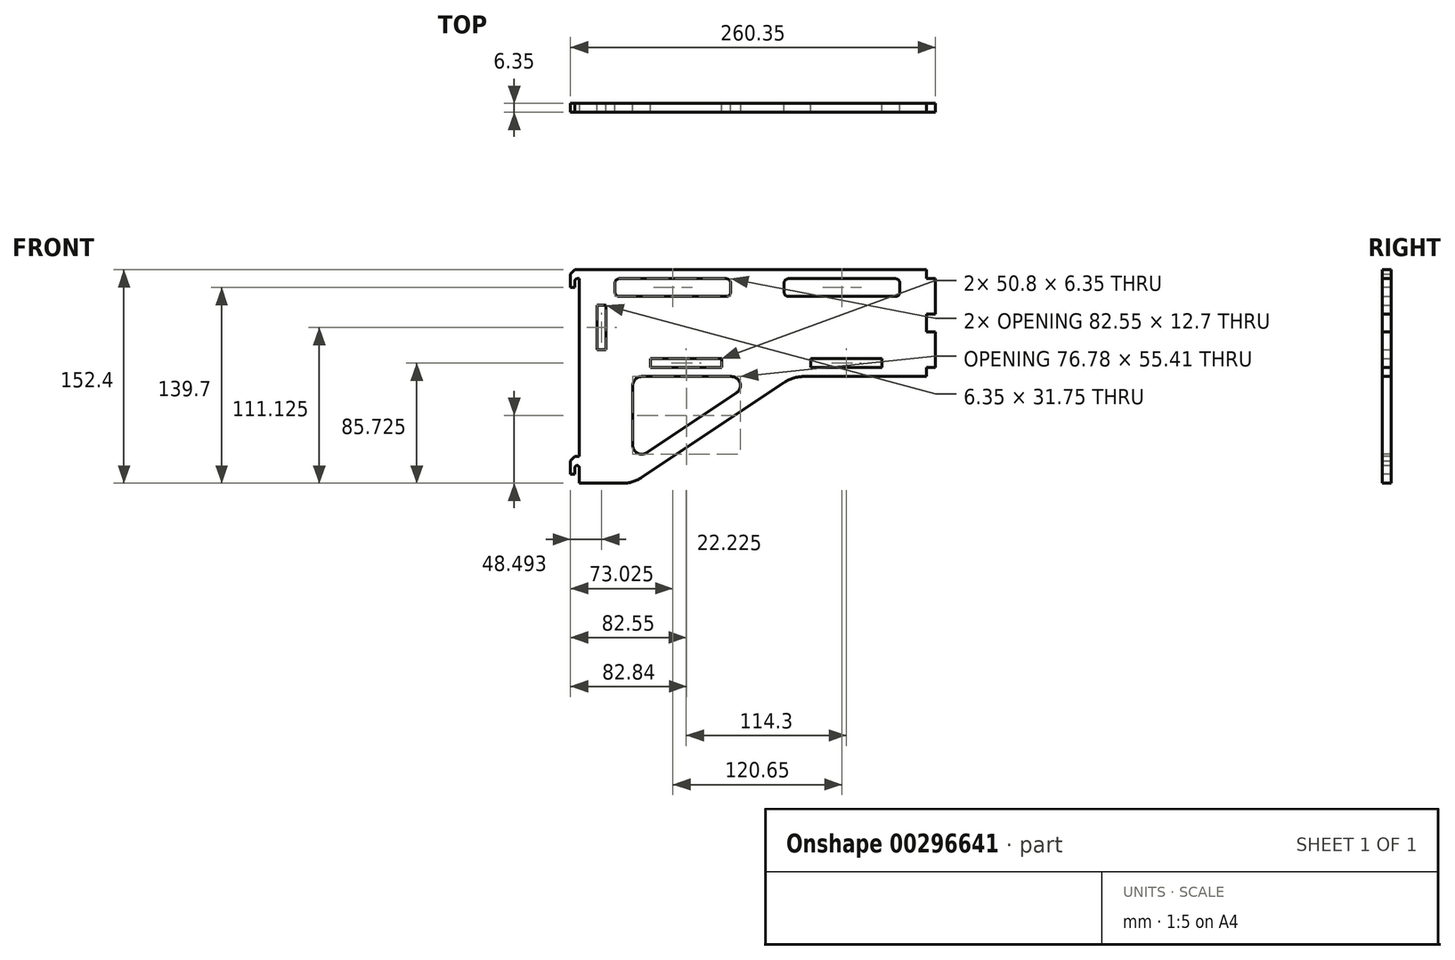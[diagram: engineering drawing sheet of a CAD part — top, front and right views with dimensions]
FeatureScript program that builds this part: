
annotation { "Feature Type Name" : "Feature", "Feature Type Description" : "" }
export const myFeature = defineFeature(function(context is Context, id is Id, definition is map)
    precondition{}
    {
        {
            var Q0;
            Q0=qCreatedBy(makeId("Front.planeOp"),FACE);
            var sketch = newSketch(context, id + "F0", { "sketchPlane" : qUnion([Q0])});
            skLineSegment(sketch, "E0.bottom", {"start": v(-127, 76.2) * mm, "end": v(120.65, 76.2) * mm});
            skLineSegment(sketch, "E0.top", {"start": v(-127, -76.2) * mm, "end": v(-88.9, -76.2) * mm});
            skLineSegment(sketch, "E0.left", {"start": v(-127, 76.2) * mm, "end": v(-127, -76.2) * mm});
            skLineSegment(sketch, "E0.right", {"start": v(127, 69.85) * mm, "end": v(127, 44.45) * mm});
            skPoint(sketch, "E0.middle", {"position": v(0, 0) * mm});
            skLineSegment(sketch, "E1", {"start": v(-88.9, -76.2) * mm, "end": v(25.4, 0) * mm});
            skLineSegment(sketch, "E2", {"start": v(25.4, 0) * mm, "end": v(120.65, 0) * mm});
            skPoint(sketch, "E3.orphan", {"position": v(127, -76.2) * mm});
            skPoint(sketch, "E4", {"position": v(0, 76.2) * mm});
            skPoint(sketch, "E5", {"position": v(-127, 0) * mm});
            skLineSegment(sketch, "E6.bottom", {"start": v(127, 69.85) * mm, "end": v(120.65, 69.85) * mm});
            skLineSegment(sketch, "E6.top", {"start": v(127, 44.45) * mm, "end": v(120.65, 44.45) * mm});
            skLineSegment(sketch, "E7.bottom", {"start": v(127, 31.75) * mm, "end": v(120.65, 31.75) * mm});
            skLineSegment(sketch, "E7.top", {"start": v(127, 6.35) * mm, "end": v(120.65, 6.35) * mm});
            skLineSegment(sketch, "E7.left", {"start": v(127, 31.75) * mm, "end": v(127, 6.35) * mm});
            skLineSegment(sketch, "E8", {"start": v(127, 38.1) * mm, "end": v(-127, 38.1) * mm, "construction": true});
            skLineSegment(sketch, "E9", {"start": v(120.65, 76.2) * mm, "end": v(120.65, 69.85) * mm});
            skPoint(sketch, "E10.orphan", {"position": v(127, 0) * mm});
            skPoint(sketch, "E11.orphan", {"position": v(127, 76.2) * mm});
            skLineSegment(sketch, "E12.trimOffspring", {"start": v(120.65, 44.45) * mm, "end": v(120.65, 31.75) * mm});
            skLineSegment(sketch, "E13.trimOffspring", {"start": v(120.65, 6.35) * mm, "end": v(120.65, 0) * mm});
            skPoint(sketch, "E14", {"position": v(127, 57.15) * mm});
            skPoint(sketch, "E15", {"position": v(127, 19.05) * mm});
            skLineSegment(sketch, "E16", {"start": v(127, 9.53) * mm, "end": v(-127, 9.52) * mm, "construction": true});
            skLineSegment(sketch, "E17.bottom", {"start": v(38.1, 12.7) * mm, "end": v(88.9, 12.7) * mm});
            skLineSegment(sketch, "E17.top", {"start": v(38.1, 6.35) * mm, "end": v(88.9, 6.35) * mm});
            skLineSegment(sketch, "E17.left", {"start": v(38.1, 12.7) * mm, "end": v(38.1, 6.35) * mm});
            skLineSegment(sketch, "E17.right", {"start": v(88.9, 12.7) * mm, "end": v(88.9, 6.35) * mm});
            skPoint(sketch, "E17.middle", {"position": v(63.5, 9.53) * mm});
            skLineSegment(sketch, "E18.bottom", {"start": v(-25.4, 12.7) * mm, "end": v(-76.2, 12.7) * mm});
            skLineSegment(sketch, "E18.top", {"start": v(-25.4, 6.35) * mm, "end": v(-76.2, 6.35) * mm});
            skLineSegment(sketch, "E18.left", {"start": v(-25.4, 12.7) * mm, "end": v(-25.4, 6.35) * mm});
            skLineSegment(sketch, "E18.right", {"start": v(-76.2, 12.7) * mm, "end": v(-76.2, 6.35) * mm});
            skPoint(sketch, "E18.middle", {"position": v(-50.8, 9.52) * mm});
            skLineSegment(sketch, "E19", {"start": v(-88.9, -60.94) * mm, "end": v(2.5, 0) * mm});
            skLineSegment(sketch, "E20", {"start": v(2.5, 0) * mm, "end": v(-88.9, 0) * mm});
            skLineSegment(sketch, "E21", {"start": v(-88.9, 0) * mm, "end": v(-88.9, -60.94) * mm});
            skLineSegment(sketch, "E22.bottom", {"start": v(-101.6, 69.85) * mm, "end": v(-19.05, 69.85) * mm});
            skLineSegment(sketch, "E22.top", {"start": v(-101.6, 57.15) * mm, "end": v(-19.05, 57.15) * mm});
            skLineSegment(sketch, "E22.left", {"start": v(-101.6, 69.85) * mm, "end": v(-101.6, 57.15) * mm});
            skLineSegment(sketch, "E22.right", {"start": v(-19.05, 69.85) * mm, "end": v(-19.05, 57.15) * mm});
            skLineSegment(sketch, "E23.MirrorCS", {"start": v(101.6, 69.85) * mm, "end": v(101.6, 57.15) * mm});
            skLineSegment(sketch, "E24.MirrorCS", {"start": v(101.6, 69.85) * mm, "end": v(19.05, 69.85) * mm});
            skLineSegment(sketch, "E25.MirrorCS", {"start": v(19.05, 69.85) * mm, "end": v(19.05, 57.15) * mm});
            skLineSegment(sketch, "E26.MirrorCS", {"start": v(101.6, 57.15) * mm, "end": v(19.05, 57.15) * mm});
            skPoint(sketch, "E27", {"position": v(6.35, 9.53) * mm});
            skPoint(sketch, "E28", {"position": v(-107.95, 9.52) * mm});
            skPoint(sketch, "E29", {"position": v(-111.13, 9.52) * mm});
            skLineSegment(sketch, "E30", {"start": v(-111.13, 76.2) * mm, "end": v(-111.13, -76.2) * mm, "construction": true});
            skLineSegment(sketch, "E31.bottom", {"start": v(-114.3, 50.8) * mm, "end": v(-107.95, 50.8) * mm});
            skLineSegment(sketch, "E31.top", {"start": v(-114.3, 19.05) * mm, "end": v(-107.95, 19.05) * mm});
            skLineSegment(sketch, "E31.left", {"start": v(-114.3, 50.8) * mm, "end": v(-114.3, 19.05) * mm});
            skLineSegment(sketch, "E31.right", {"start": v(-107.95, 50.8) * mm, "end": v(-107.95, 19.05) * mm});
            skPoint(sketch, "E31.middle", {"position": v(-111.13, 34.92) * mm});
            skSolve(sketch);
        }
        {
            var Q0;
            Q0 = qSketchRegion(id + "F0", true);
            extrude(context, id + "F1", {"entities" : qUnion([Q0]), "depth" : 6.35 * mm});
        }
        {
            var Q0;
            Q0=makeQuery(id+"F1.opExtrude","SWEPT_EDGE",EDGE,{"disambiguationData":[OSD([sQuery(id+"F0.wireOp",EDGE,"E19"),sQuery(id+"F0.wireOp",EDGE,"E20")])]});
            var Q1;
            Q1=makeQuery(id+"F1.opExtrude","SWEPT_EDGE",EDGE,{"disambiguationData":[OSD([sQuery(id+"F0.wireOp",EDGE,"E19"),sQuery(id+"F0.wireOp",EDGE,"E21")])]});
            var Q2;
            Q2=makeQuery(id+"F1.opExtrude","SWEPT_EDGE",EDGE,{"disambiguationData":[OSD([sQuery(id+"F0.wireOp",EDGE,"E20"),sQuery(id+"F0.wireOp",EDGE,"E21")])]});
            fillet(context, id + "F2", {"entities" : qUnion([Q0, Q1, Q2]), "radius" : 6.35 * mm, "tangentPropagation" : true, "allowEdgeOverflow" : false});
        }
        {
            var Q0;
            Q0=makeQuery(id+"F1.opExtrude","SWEPT_EDGE",EDGE,{"disambiguationData":[OSD([sQuery(id+"F0.wireOp",EDGE,"E1"),sQuery(id+"F0.wireOp",EDGE,"E2")])]});
            var Q1;
            Q1=makeQuery(id+"F1.opExtrude","SWEPT_EDGE",EDGE,{"disambiguationData":[OSD([sQuery(id+"F0.wireOp",EDGE,"E0.top"),sQuery(id+"F0.wireOp",EDGE,"E1")])]});
            fillet(context, id + "F3", {"entities" : qUnion([Q0, Q1]), "radius" : 25.4 * mm, "tangentPropagation" : true, "allowEdgeOverflow" : false});
        }
        {
            var Q0;
            Q0=makeQuery(id+"F1.opExtrude","SWEPT_EDGE",EDGE,{"disambiguationData":[OSD([sQuery(id+"F0.wireOp",EDGE,"E22.top"),sQuery(id+"F0.wireOp",EDGE,"E22.left")])]});
            var Q1;
            Q1=makeQuery(id+"F1.opExtrude","SWEPT_EDGE",EDGE,{"disambiguationData":[OSD([sQuery(id+"F0.wireOp",EDGE,"E22.bottom"),sQuery(id+"F0.wireOp",EDGE,"E22.left")])]});
            var Q2;
            Q2=makeQuery(id+"F1.opExtrude","SWEPT_EDGE",EDGE,{"disambiguationData":[OSD([sQuery(id+"F0.wireOp",EDGE,"E22.top"),sQuery(id+"F0.wireOp",EDGE,"E22.right")])]});
            var Q3;
            Q3=makeQuery(id+"F1.opExtrude","SWEPT_EDGE",EDGE,{"disambiguationData":[OSD([sQuery(id+"F0.wireOp",EDGE,"E22.bottom"),sQuery(id+"F0.wireOp",EDGE,"E22.right")])]});
            var Q4;
            Q4=makeQuery(id+"F1.opExtrude","SWEPT_EDGE",EDGE,{"disambiguationData":[OSD([sQuery(id+"F0.wireOp",EDGE,"E23.MirrorCS"),sQuery(id+"F0.wireOp",EDGE,"E24.MirrorCS")])]});
            var Q5;
            Q5=makeQuery(id+"F1.opExtrude","SWEPT_EDGE",EDGE,{"disambiguationData":[OSD([sQuery(id+"F0.wireOp",EDGE,"E23.MirrorCS"),sQuery(id+"F0.wireOp",EDGE,"E26.MirrorCS")])]});
            var Q6;
            Q6=makeQuery(id+"F1.opExtrude","SWEPT_EDGE",EDGE,{"disambiguationData":[OSD([sQuery(id+"F0.wireOp",EDGE,"E25.MirrorCS"),sQuery(id+"F0.wireOp",EDGE,"E26.MirrorCS")])]});
            var Q7;
            Q7=makeQuery(id+"F1.opExtrude","SWEPT_EDGE",EDGE,{"disambiguationData":[OSD([sQuery(id+"F0.wireOp",EDGE,"E24.MirrorCS"),sQuery(id+"F0.wireOp",EDGE,"E25.MirrorCS")])]});
            fillet(context, id + "F4", {"entities" : qUnion([Q0, Q1, Q2, Q3, Q4, Q5, Q6, Q7]), "radius" : 3.17 * mm, "tangentPropagation" : true, "allowEdgeOverflow" : false});
        }
        {
            var Q0;
            Q0=makeQuery(id+"F1.opExtrude","CAP_FACE",FACE,{"disambiguationData":[OSD([sQuery(id+"F0.wireOp",EDGE,"E0.bottom"),sQuery(id+"F0.wireOp",EDGE,"E0.top"),sQuery(id+"F0.wireOp",EDGE,"E0.left"),sQuery(id+"F0.wireOp",EDGE,"E1"),sQuery(id+"F0.wireOp",EDGE,"E2"),sQuery(id+"F0.wireOp",EDGE,"E6.bottom"),sQuery(id+"F0.wireOp",EDGE,"E6.top"),sQuery(id+"F0.wireOp",EDGE,"E0.right"),sQuery(id+"F0.wireOp",EDGE,"E7.bottom"),sQuery(id+"F0.wireOp",EDGE,"E7.top"),sQuery(id+"F0.wireOp",EDGE,"E9"),sQuery(id+"F0.wireOp",EDGE,"E7.left"),sQuery(id+"F0.wireOp",EDGE,"E12.trimOffspring"),sQuery(id+"F0.wireOp",EDGE,"E13.trimOffspring"),sQuery(id+"F0.wireOp",EDGE,"E17.bottom"),sQuery(id+"F0.wireOp",EDGE,"E17.top"),sQuery(id+"F0.wireOp",EDGE,"E17.left"),sQuery(id+"F0.wireOp",EDGE,"E17.right"),sQuery(id+"F0.wireOp",EDGE,"E18.bottom"),sQuery(id+"F0.wireOp",EDGE,"E18.top"),sQuery(id+"F0.wireOp",EDGE,"E18.left"),sQuery(id+"F0.wireOp",EDGE,"E18.right"),sQuery(id+"F0.wireOp",EDGE,"E19"),sQuery(id+"F0.wireOp",EDGE,"E20"),sQuery(id+"F0.wireOp",EDGE,"E21"),sQuery(id+"F0.wireOp",EDGE,"E22.bottom"),sQuery(id+"F0.wireOp",EDGE,"E22.top"),sQuery(id+"F0.wireOp",EDGE,"E22.left"),sQuery(id+"F0.wireOp",EDGE,"E22.right"),sQuery(id+"F0.wireOp",EDGE,"E23.MirrorCS"),sQuery(id+"F0.wireOp",EDGE,"E24.MirrorCS"),sQuery(id+"F0.wireOp",EDGE,"E25.MirrorCS"),sQuery(id+"F0.wireOp",EDGE,"E26.MirrorCS"),sQuery(id+"F0.wireOp",EDGE,"E31.bottom"),sQuery(id+"F0.wireOp",EDGE,"E31.top"),sQuery(id+"F0.wireOp",EDGE,"E31.left"),sQuery(id+"F0.wireOp",EDGE,"E31.right")])],"isStart":false});
            var sketch = newSketch(context, id + "F5", { "sketchPlane" : qUnion([Q0])});
            skLineSegment(sketch, "E32", {"start": v(-127, 76.2) * mm, "end": v(-133.35, 76.2) * mm});
            skLineSegment(sketch, "E33", {"start": v(-133.35, 76.2) * mm, "end": v(-133.35, 63.5) * mm});
            skLineSegment(sketch, "E34", {"start": v(-133.35, 63.5) * mm, "end": v(-130.18, 63.5) * mm});
            skLineSegment(sketch, "E35", {"start": v(-130.18, 63.5) * mm, "end": v(-130.18, 69.85) * mm});
            skLineSegment(sketch, "E36", {"start": v(-130.18, 69.85) * mm, "end": v(-127, 69.85) * mm});
            skLineSegment(sketch, "E37", {"start": v(-127, 76.2) * mm, "end": v(-127, 69.85) * mm});
            skLineSegment(sketch, "E38", {"start": v(-127, -63.5) * mm, "end": v(-130.18, -63.5) * mm});
            skLineSegment(sketch, "E39", {"start": v(-130.18, -63.5) * mm, "end": v(-130.18, -69.85) * mm});
            skLineSegment(sketch, "E40", {"start": v(-130.18, -69.85) * mm, "end": v(-133.35, -69.85) * mm});
            skLineSegment(sketch, "E41", {"start": v(-133.35, -69.85) * mm, "end": v(-133.35, -57.15) * mm});
            skLineSegment(sketch, "E42", {"start": v(-133.35, -57.15) * mm, "end": v(-127, -57.15) * mm});
            skLineSegment(sketch, "E43", {"start": v(-127, -63.5) * mm, "end": v(-127, -57.15) * mm});
            skSolve(sketch);
        }
        {
            var Q0;
            Q0 = qSketchRegion(id + "F5", true);
            var Q1;
            {var subQ0=sQuery(id+"F5.wireOp",EDGE,"E38");Q1=makeQuery(id+"F5.imprint","IMPRINT",FACE,{"disambiguationData":[TD([[makeQuery(id+"F5.imprint","IMPRINT",EDGE,{"derivedFrom":subQ0}),-1.0]])]});}
            extrude(context, id + "F6", {"entities" : qUnion([Q0, Q1]), "operationType" : NewBodyOperationType.ADD, "oppositeDirection" : true, "depth" : 6.35 * mm});
        }
        {
            var Q0;
            Q0=makeQuery(id+"F6.opExtrude","SWEPT_EDGE",EDGE,{"disambiguationData":[OSD([sQuery(id+"F0.wireOp",EDGE,"E0.left"),sQuery(id+"F5.wireOp",EDGE,"E36"),sQuery(id+"F5.wireOp",EDGE,"E37")])]});
            var Q1;
            Q1=makeQuery(id+"F6.opExtrude","SWEPT_EDGE",EDGE,{"disambiguationData":[OSD([sQuery(id+"F5.wireOp",EDGE,"E35"),sQuery(id+"F5.wireOp",EDGE,"E36")])]});
            var Q2;
            Q2=makeQuery(id+"F6.opExtrude","SWEPT_EDGE",EDGE,{"disambiguationData":[OSD([sQuery(id+"F5.wireOp",EDGE,"E38"),sQuery(id+"F5.wireOp",EDGE,"E39")])]});
            var Q3;
            Q3=makeQuery(id+"F6.opExtrude","SWEPT_EDGE",EDGE,{"disambiguationData":[OSD([sQuery(id+"F0.wireOp",EDGE,"E0.left"),sQuery(id+"F5.wireOp",EDGE,"E38"),sQuery(id+"F5.wireOp",EDGE,"E43")])]});
            fillet(context, id + "F7", {"entities" : qUnion([Q0, Q1, Q2, Q3]), "radius" : 1.59 * mm, "tangentPropagation" : true, "allowEdgeOverflow" : false});
        }
        {
            var Q0;
            Q0=makeQuery(id+"F6.opExtrude","SWEPT_EDGE",EDGE,{"disambiguationData":[OSD([sQuery(id+"F5.wireOp",EDGE,"E32"),sQuery(id+"F5.wireOp",EDGE,"E33")])]});
            var Q1;
            Q1=makeQuery(id+"F6.opExtrude","SWEPT_EDGE",EDGE,{"disambiguationData":[OSD([sQuery(id+"F5.wireOp",EDGE,"E41"),sQuery(id+"F5.wireOp",EDGE,"E42")])]});
            chamfer(context, id + "F8", {"entities" : qUnion([Q0, Q1]), "width" : 3.17 * mm, "tangentPropagation" : true});
        }
    });
